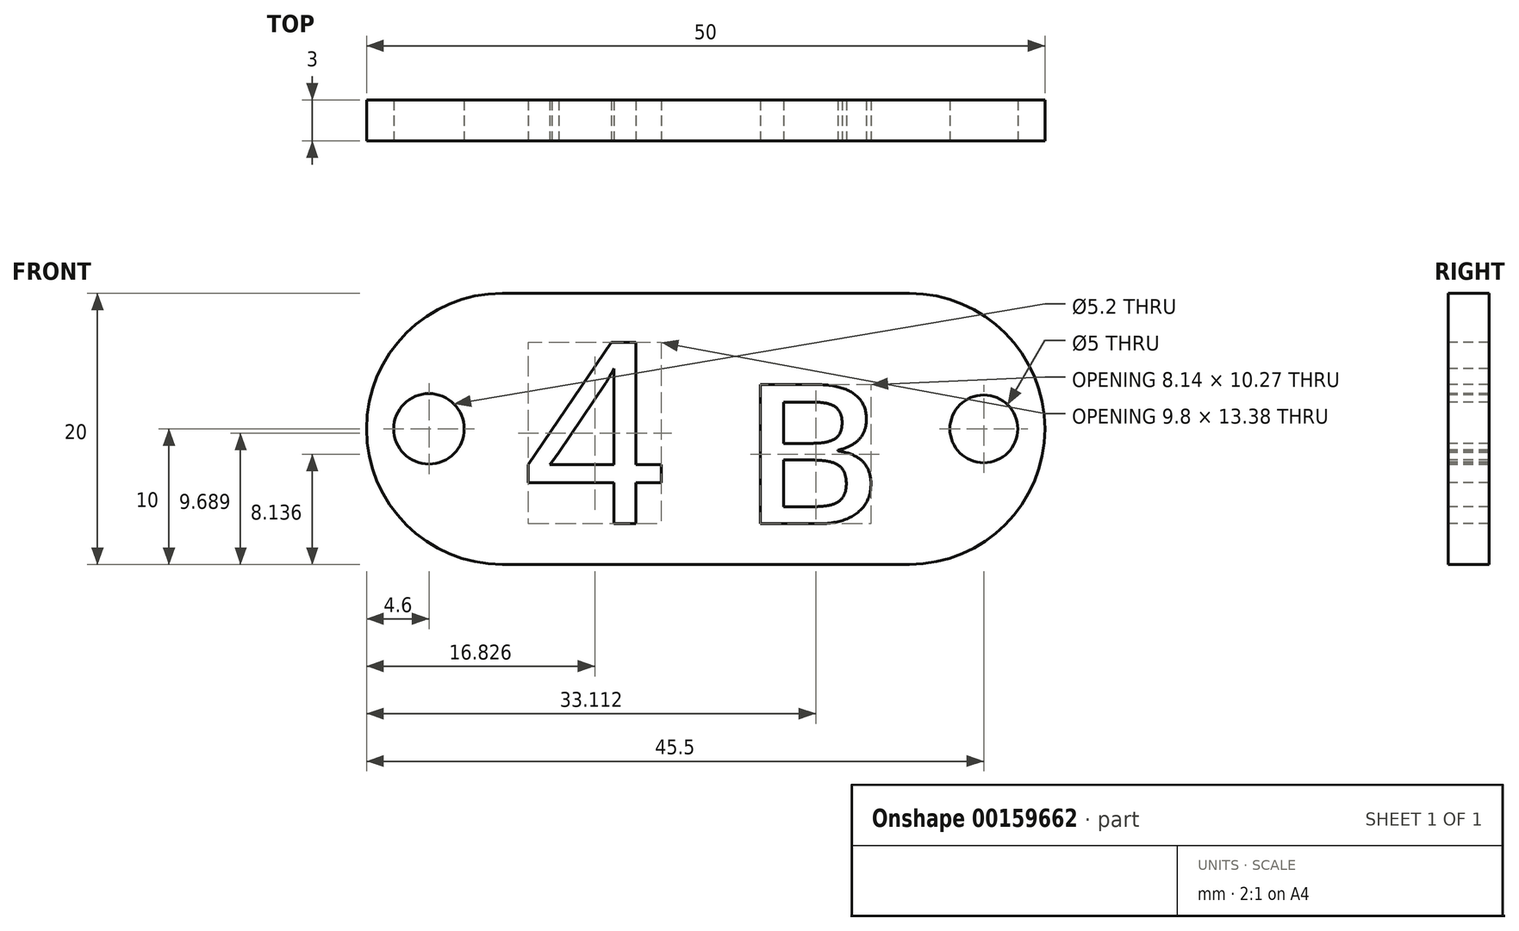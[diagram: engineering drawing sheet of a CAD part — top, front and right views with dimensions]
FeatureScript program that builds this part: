
annotation { "Feature Type Name" : "Feature", "Feature Type Description" : "" }
export const myFeature = defineFeature(function(context is Context, id is Id, definition is map)
    precondition{}
    {
        {
            var Q0;
            Q0=qCreatedBy(makeId("Front.planeOp"),FACE);
            var sketch = newSketch(context, id + "F0", { "sketchPlane" : qUnion([Q0])});
            skLineSegment(sketch, "E0.bottom", {"start": v(25, 10) * mm, "end": v(-25, 10) * mm});
            skLineSegment(sketch, "E0.top", {"start": v(25, -10) * mm, "end": v(-25, -10) * mm});
            skLineSegment(sketch, "E0.left", {"start": v(25, 10) * mm, "end": v(25, -10) * mm});
            skLineSegment(sketch, "E0.right", {"start": v(-25, 10) * mm, "end": v(-25, -10) * mm});
            skPoint(sketch, "E0.middle", {"position": v(0, 0) * mm});
            skSolve(sketch);
        }
        {
            var Q0;
            Q0=makeQuery(id+"F0.imprint","IMPRINT",FACE,{"disambiguationData":[TD([[makeQuery(id+"F0.imprint","IMPRINT",EDGE,{"derivedFrom":sQuery(id+"F0.wireOp",EDGE,"E0.bottom")}),1.0]])]});
            extrude(context, id + "F1", {"entities" : qUnion([Q0]), "depth" : 3 * mm});
        }
        {
            var Q0;
            Q0=makeQuery(id+"F1.opExtrude","CAP_FACE",FACE,{"disambiguationData":[OSD([sQuery(id+"F0.wireOp",EDGE,"E0.bottom"),sQuery(id+"F0.wireOp",EDGE,"E0.top"),sQuery(id+"F0.wireOp",EDGE,"E0.left"),sQuery(id+"F0.wireOp",EDGE,"E0.right")])],"isStart":false});
            var sketch = newSketch(context, id + "F2", { "sketchPlane" : qUnion([Q0])});
            skText(sketch, "E1", { "text": "4 в", "fontName": "Arimo-Regular.ttf"});
            skLineSegment(sketch, "E2", {"start": v(-13.52, 0) * mm, "end": v(13.52, 0) * mm, "construction": true});
            skPoint(sketch, "E3", {"position": v(0, 0) * mm});
            skCircle(sketch, "E4", {"center": v(20.5, 0) * mm, "radius": 2.5 * mm});
            skCircle(sketch, "E5", {"center": v(-20.4, 0) * mm, "radius": 2.6 * mm});
            const initialGuessF2  = {"E1": [-0.01352, -0.007, 1, 0, 0.014]};
            skSetInitialGuess(sketch, initialGuessF2);
            skSolve(sketch);
        }
        {
            var Q0;
            Q0=qSketchRegion(id+"F2",true);
            extrude(context, id + "F3", {"entities" : qUnion([Q0]), "operationType" : NewBodyOperationType.REMOVE, "endBound" : BoundingType.THROUGH_ALL, "oppositeDirection" : true, "depth" : 25 * mm});
        }
        {
            var Q0;
            Q0=makeQuery(id+"F1.opExtrude","SWEPT_EDGE",EDGE,{"disambiguationData":[OSD([sQuery(id+"F0.wireOp",EDGE,"E0.bottom"),sQuery(id+"F0.wireOp",EDGE,"E0.right")])]});
            var Q1;
            Q1=makeQuery(id+"F1.opExtrude","SWEPT_EDGE",EDGE,{"disambiguationData":[OSD([sQuery(id+"F0.wireOp",EDGE,"E0.top"),sQuery(id+"F0.wireOp",EDGE,"E0.right")])]});
            var Q2;
            Q2=makeQuery(id+"F1.opExtrude","SWEPT_EDGE",EDGE,{"disambiguationData":[OSD([sQuery(id+"F0.wireOp",EDGE,"E0.bottom"),sQuery(id+"F0.wireOp",EDGE,"E0.left")])]});
            var Q3;
            Q3=makeQuery(id+"F1.opExtrude","SWEPT_EDGE",EDGE,{"disambiguationData":[OSD([sQuery(id+"F0.wireOp",EDGE,"E0.top"),sQuery(id+"F0.wireOp",EDGE,"E0.left")])]});
            fillet(context, id + "F4", {"entities" : qUnion([Q0, Q1, Q2, Q3]), "radius" : 10 * mm, "tangentPropagation" : true, "allowEdgeOverflow" : false});
        }
    });
